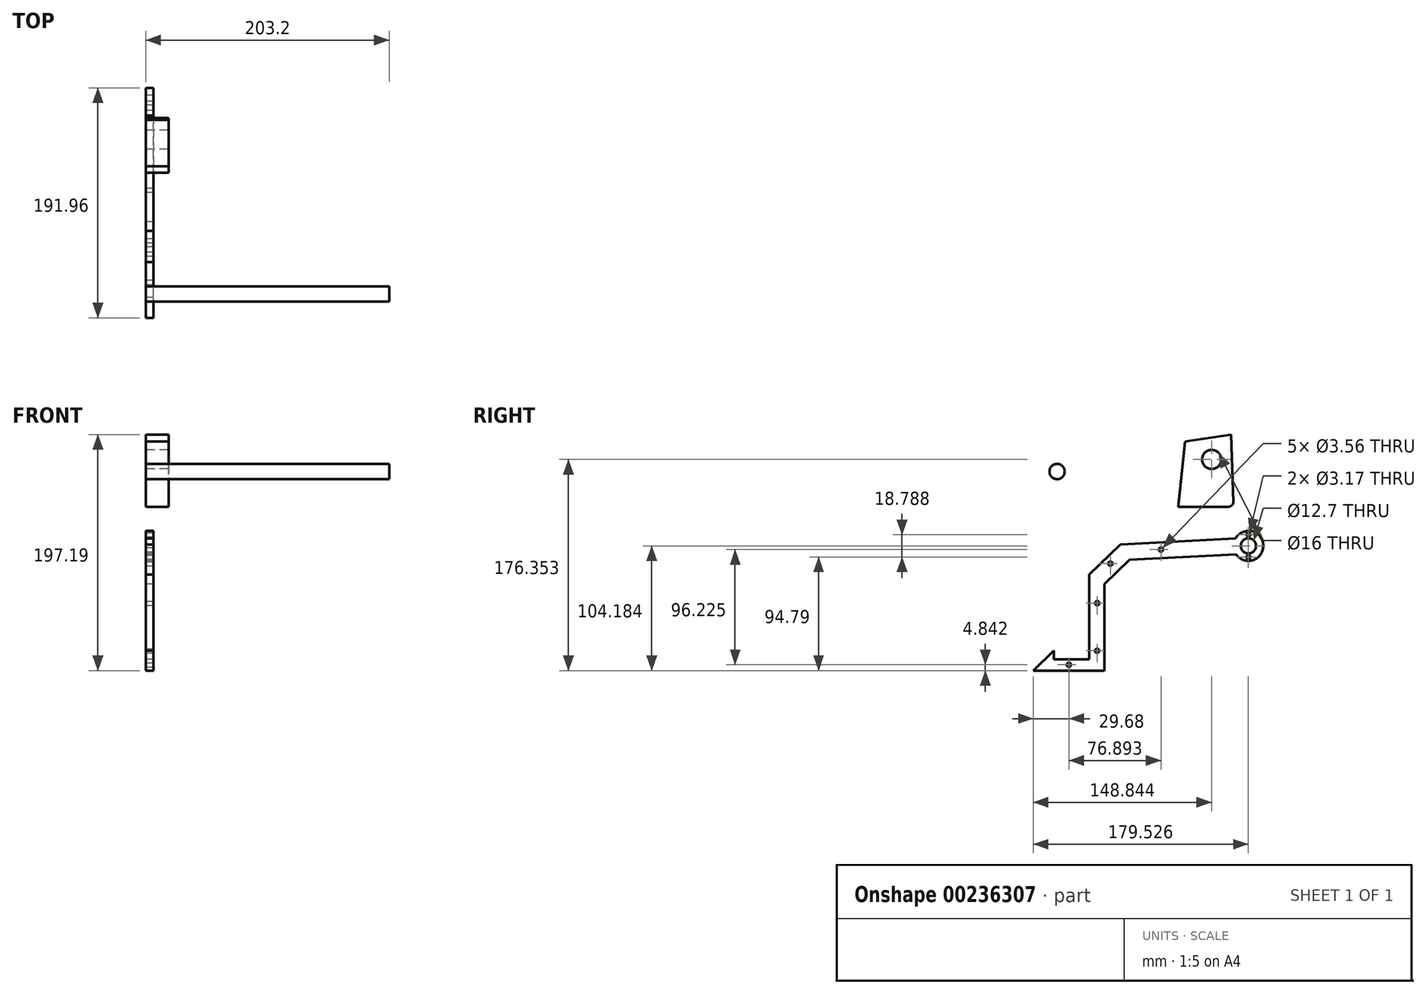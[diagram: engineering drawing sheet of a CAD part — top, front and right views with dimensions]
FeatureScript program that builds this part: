
annotation { "Feature Type Name" : "Feature", "Feature Type Description" : "" }
export const myFeature = defineFeature(function(context is Context, id is Id, definition is map)
    precondition{}
    {
        {
            var Q0;
            Q0=qCreatedBy(makeId("Right.planeOp"),FACE);
            var sketch = newSketch(context, id + "F0", { "sketchPlane" : qUnion([Q0])});
            skLineSegment(sketch, "E0", {"start": v(31.36, 3.92) * mm, "end": v(29.67, 60.32) * mm});
            skLineSegment(sketch, "E1", {"start": v(29.67, 60.32) * mm, "end": v(-8.9, 54.49) * mm});
            skLineSegment(sketch, "E2", {"start": v(-8.9, 54.49) * mm, "end": v(-14.47, 0) * mm});
            skLineSegment(sketch, "E3", {"start": v(-14.47, 0) * mm, "end": v(27.55, 0) * mm});
            skPoint(sketch, "E4.visualSharp", {"position": v(31.48, 0) * mm});
            skArc(sketch, "E4.filletArc", {"start": v(27.55, 0) * mm, "mid": v(30.28, 1.16) * mm, "end": v(31.36, 3.92) * mm});
            skCircle(sketch, "E5", {"center": v(13.31, 39.48) * mm, "radius": 8 * mm});
            skSolve(sketch);
        }
        {
            var Q0;
            Q0=makeQuery(id+"F0.imprint","IMPRINT",FACE,{"disambiguationData":[TD([[makeQuery(id+"F0.imprint","IMPRINT",EDGE,{"derivedFrom":sQuery(id+"F0.wireOp",EDGE,"E0")}),1.0]])]});
            extrude(context, id + "F1", {"entities" : qUnion([Q0]), "depth" : 19.05 * mm});
        }
        {
            var Q0;
            Q0=qCreatedBy(makeId("Right.planeOp"),FACE);
            var sketch = newSketch(context, id + "F2", { "sketchPlane" : qUnion([Q0])});
            skLineSegment(sketch, "E6", {"start": v(63.8, -38.23) * mm, "end": v(-55.35, -44.32) * mm});
            skLineSegment(sketch, "E7", {"start": v(-55.35, -44.32) * mm, "end": v(-76.17, -64.48) * mm});
            skLineSegment(sketch, "E8", {"start": v(-76.17, -64.48) * mm, "end": v(-76.17, -136.87) * mm});
            skLineSegment(sketch, "E9", {"start": v(-76.17, -136.87) * mm, "end": v(-135.53, -136.87) * mm});
            skLineSegment(sketch, "E10", {"start": v(-135.53, -136.87) * mm, "end": v(-118.4, -120.3) * mm});
            skLineSegment(sketch, "E11", {"start": v(-118.4, -120.3) * mm, "end": v(-118.4, -127.34) * mm});
            skLineSegment(sketch, "E12", {"start": v(-118.4, -127.34) * mm, "end": v(-88.87, -127.34) * mm});
            skLineSegment(sketch, "E13", {"start": v(-88.87, -127.34) * mm, "end": v(-88.87, -56.55) * mm});
            skLineSegment(sketch, "E14", {"start": v(-88.87, -56.55) * mm, "end": v(-62.9, -31.4) * mm});
            skLineSegment(sketch, "E15", {"start": v(-62.9, -31.4) * mm, "end": v(63.8, -24.93) * mm});
            skCircle(sketch, "E16", {"center": v(44, -32.69) * mm, "radius": 12.44 * mm});
            skCircle(sketch, "E17", {"center": v(44, -32.69) * mm, "radius": 6.35 * mm});
            skSolve(sketch);
        }
        {
            var Q0;
            Q0 = qSketchRegion(id + "F2", true);
            extrude(context, id + "F3", {"entities" : qUnion([Q0]), "depth" : 6.35 * mm});
        }
        {
            var Q0;
            Q0=qCreatedBy(makeId("Right.planeOp"),FACE);
            var sketch = newSketch(context, id + "F4", { "sketchPlane" : qUnion([Q0])});
            skCircle(sketch, "E18", {"center": v(-115.7, 29.39) * mm, "radius": 6.35 * mm});
            skSolve(sketch);
        }
        {
            var Q0;
            Q0 = qSketchRegion(id + "F4", true);
            extrude(context, id + "F9", {"entities" : qUnion([Q0]), "depth" : 203.2 * mm});
        }
        {
            var Q0;
            Q0=makeQuery(id+"F3.opExtrude","CAP_FACE",FACE,{"disambiguationData":[OSD([sQuery(id+"F2.wireOp",EDGE,"E6"),sQuery(id+"F2.wireOp",EDGE,"E7"),sQuery(id+"F2.wireOp",EDGE,"E8"),sQuery(id+"F2.wireOp",EDGE,"E9"),sQuery(id+"F2.wireOp",EDGE,"E10"),sQuery(id+"F2.wireOp",EDGE,"E11"),sQuery(id+"F2.wireOp",EDGE,"E12"),sQuery(id+"F2.wireOp",EDGE,"E13"),sQuery(id+"F2.wireOp",EDGE,"E14"),sQuery(id+"F2.wireOp",EDGE,"E15"),sQuery(id+"F2.wireOp",EDGE,"E16"),sQuery(id+"F2.wireOp",EDGE,"E17")])],"isStart":false});
            var sketch = newSketch(context, id + "F5", { "sketchPlane" : qUnion([Q0])});
            skLineSegment(sketch, "E19", {"start": v(44, -32.69) * mm, "end": v(44, -26.34) * mm});
            skLineSegment(sketch, "E20", {"start": v(44, -26.34) * mm, "end": v(44, -20.25) * mm});
            skLineSegment(sketch, "E21", {"start": v(44, -32.69) * mm, "end": v(44, -39.04) * mm});
            skLineSegment(sketch, "E22", {"start": v(44, -39.04) * mm, "end": v(44, -45.12) * mm});
            skCircle(sketch, "E23", {"center": v(44, -42.08) * mm, "radius": 1.59 * mm});
            skCircle(sketch, "E24", {"center": v(44, -23.3) * mm, "radius": 1.59 * mm});
            skSolve(sketch);
        }
        {
            var Q0;
            Q0 = qSketchRegion(id + "F5", true);
            extrude(context, id + "F6", {"entities" : qUnion([Q0]), "operationType" : NewBodyOperationType.REMOVE, "endBound" : BoundingType.THROUGH_ALL, "oppositeDirection" : true, "depth" : 25.4 * mm});
        }
        {
            var Q0;
            Q0=makeQuery(id+"F3.opExtrude","CAP_FACE",FACE,{"disambiguationData":[OSD([sQuery(id+"F2.wireOp",EDGE,"E6"),sQuery(id+"F2.wireOp",EDGE,"E7"),sQuery(id+"F2.wireOp",EDGE,"E8"),sQuery(id+"F2.wireOp",EDGE,"E9"),sQuery(id+"F2.wireOp",EDGE,"E10"),sQuery(id+"F2.wireOp",EDGE,"E11"),sQuery(id+"F2.wireOp",EDGE,"E12"),sQuery(id+"F2.wireOp",EDGE,"E13"),sQuery(id+"F2.wireOp",EDGE,"E14"),sQuery(id+"F2.wireOp",EDGE,"E15"),sQuery(id+"F2.wireOp",EDGE,"E16"),sQuery(id+"F2.wireOp",EDGE,"E17")])],"isStart":false});
            var sketch = newSketch(context, id + "F7", { "sketchPlane" : qUnion([Q0])});
            skCircle(sketch, "E25", {"center": v(-105.85, -132.03) * mm, "radius": 1.78 * mm});
            skPoint(sketch, "E25.centerSnap0", {"position": v(-105.85, -136.87) * mm});
            skCircle(sketch, "E26", {"center": v(-82.24, -120.3) * mm, "radius": 1.78 * mm});
            skCircle(sketch, "E27", {"center": v(-82.24, -80.59) * mm, "radius": 1.78 * mm});
            skCircle(sketch, "E28", {"center": v(-28.96, -35.8) * mm, "radius": 1.78 * mm});
            skCircle(sketch, "E29", {"center": v(-71.17, -47.56) * mm, "radius": 1.78 * mm});
            skSolve(sketch);
        }
        {
            var Q0;
            Q0 = qSketchRegion(id + "F7", true);
            extrude(context, id + "F8", {"entities" : qUnion([Q0]), "operationType" : NewBodyOperationType.REMOVE, "endBound" : BoundingType.THROUGH_ALL, "oppositeDirection" : true, "depth" : 25.4 * mm});
        }
    });
